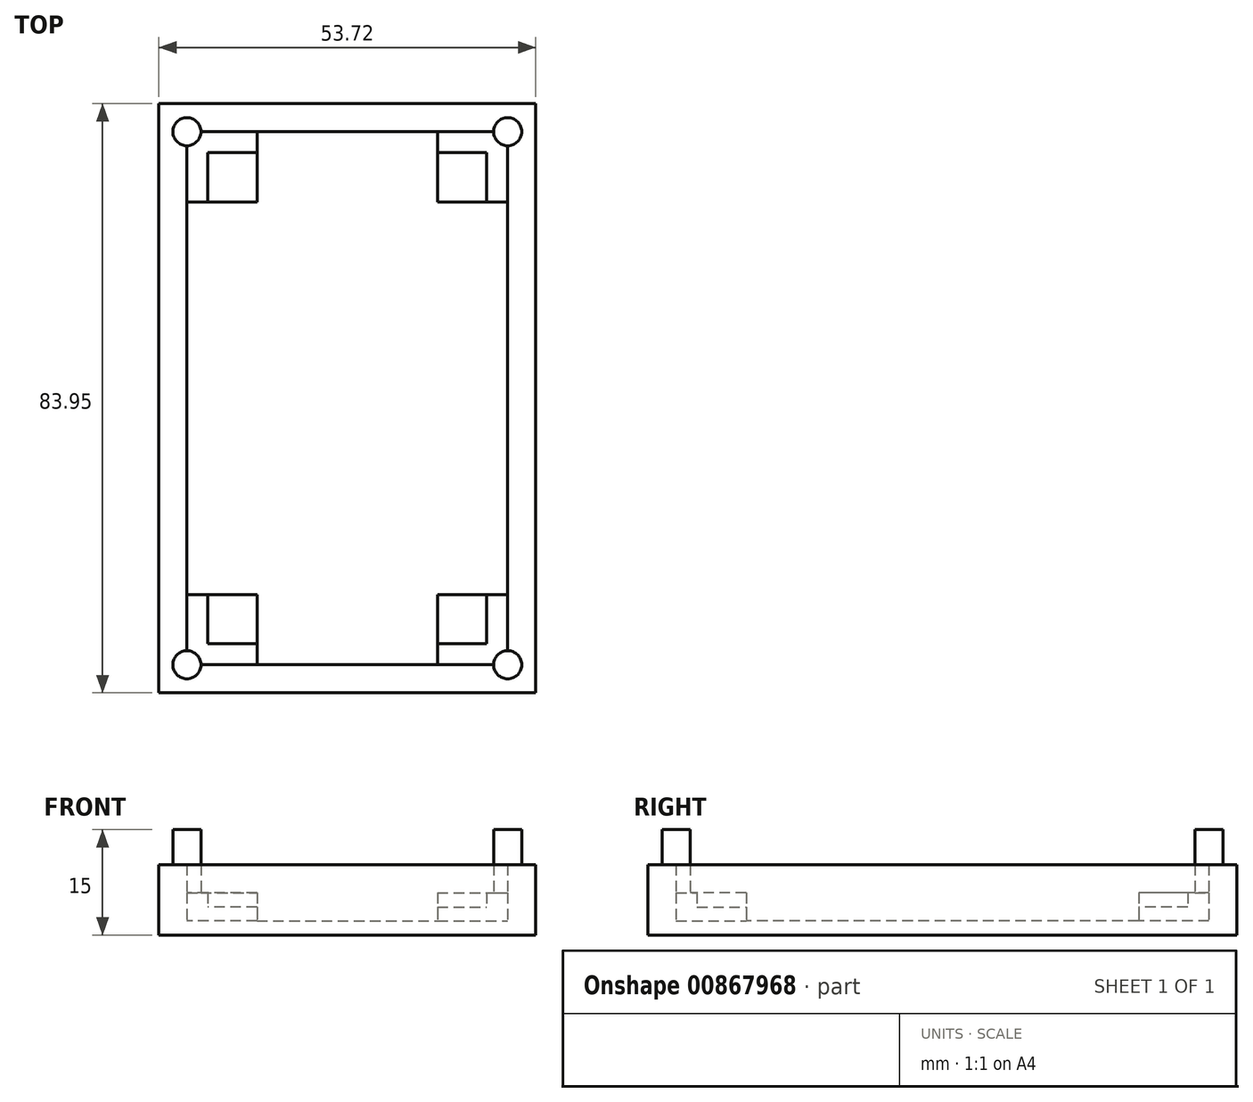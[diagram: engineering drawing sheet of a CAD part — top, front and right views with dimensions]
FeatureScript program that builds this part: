
annotation { "Feature Type Name" : "Feature", "Feature Type Description" : "" }
export const myFeature = defineFeature(function(context is Context, id is Id, definition is map)
    precondition{}
    {
        {
            var Q0;
            Q0=qCreatedBy(makeId("Top.planeOp"),FACE);
            var sketch = newSketch(context, id + "F0", { "sketchPlane" : qUnion([Q0])});
            skLineSegment(sketch, "E0.bottom", {"start": v(-27.14, 34.73) * mm, "end": v(26.58, 34.73) * mm});
            skLineSegment(sketch, "E0.top", {"start": v(-27.14, -49.22) * mm, "end": v(26.58, -49.22) * mm});
            skLineSegment(sketch, "E0.left", {"start": v(-27.14, 34.73) * mm, "end": v(-27.14, -49.22) * mm});
            skLineSegment(sketch, "E0.right", {"start": v(26.58, 34.73) * mm, "end": v(26.58, -49.22) * mm});
            skLineSegment(sketch, "E1.bottom", {"start": v(-23.14, 30.73) * mm, "end": v(22.58, 30.73) * mm});
            skLineSegment(sketch, "E1.top", {"start": v(-23.14, -45.22) * mm, "end": v(22.58, -45.22) * mm});
            skLineSegment(sketch, "E1.left", {"start": v(-23.14, 30.73) * mm, "end": v(-23.14, -45.22) * mm});
            skLineSegment(sketch, "E1.right", {"start": v(22.58, 30.73) * mm, "end": v(22.58, -45.22) * mm});
            skLineSegment(sketch, "E2", {"start": v(-23.14, 30.73) * mm, "end": v(-27.14, 30.73) * mm});
            skLineSegment(sketch, "E3", {"start": v(-23.14, 30.73) * mm, "end": v(-23.14, 34.73) * mm});
            skLineSegment(sketch, "E4", {"start": v(22.58, -45.22) * mm, "end": v(26.58, -45.22) * mm});
            skLineSegment(sketch, "E5", {"start": v(22.58, -45.22) * mm, "end": v(22.58, -49.22) * mm});
            skCircle(sketch, "E6", {"center": v(-23.14, 30.73) * mm, "radius": 2 * mm});
            skCircle(sketch, "E7", {"center": v(22.58, 30.73) * mm, "radius": 2 * mm});
            skCircle(sketch, "E8", {"center": v(22.58, -45.22) * mm, "radius": 2 * mm});
            skCircle(sketch, "E9", {"center": v(-23.14, -45.22) * mm, "radius": 2 * mm});
            skLineSegment(sketch, "E10", {"start": v(12.58, -45.22) * mm, "end": v(12.58, -35.22) * mm});
            skLineSegment(sketch, "E11", {"start": v(12.58, -35.22) * mm, "end": v(22.58, -35.22) * mm});
            skLineSegment(sketch, "E12", {"start": v(-13.14, -45.22) * mm, "end": v(-13.14, -35.22) * mm});
            skLineSegment(sketch, "E13", {"start": v(-13.14, -35.22) * mm, "end": v(-23.14, -35.22) * mm});
            skLineSegment(sketch, "E14", {"start": v(12.58, 30.73) * mm, "end": v(12.58, 20.73) * mm});
            skLineSegment(sketch, "E15", {"start": v(12.58, 20.73) * mm, "end": v(22.58, 20.73) * mm});
            skLineSegment(sketch, "E16", {"start": v(-13.14, 30.73) * mm, "end": v(-13.14, 20.73) * mm});
            skLineSegment(sketch, "E17", {"start": v(-13.14, 20.73) * mm, "end": v(-23.14, 20.73) * mm});
            skLineSegment(sketch, "E18", {"start": v(-20.14, -35.22) * mm, "end": v(-20.14, -42.22) * mm});
            skLineSegment(sketch, "E19", {"start": v(-20.14, -42.22) * mm, "end": v(-13.14, -42.22) * mm});
            skLineSegment(sketch, "E20", {"start": v(12.58, 27.73) * mm, "end": v(19.58, 27.73) * mm});
            skLineSegment(sketch, "E21", {"start": v(19.58, 27.73) * mm, "end": v(19.58, 20.73) * mm});
            skLineSegment(sketch, "E22", {"start": v(-13.14, 27.73) * mm, "end": v(-20.14, 27.73) * mm});
            skLineSegment(sketch, "E23", {"start": v(-20.14, 27.73) * mm, "end": v(-20.14, 20.73) * mm});
            skLineSegment(sketch, "E24", {"start": v(19.58, -42.22) * mm, "end": v(12.58, -42.22) * mm});
            skLineSegment(sketch, "E25", {"start": v(19.58, -42.22) * mm, "end": v(19.58, -35.22) * mm});
            skSolve(sketch);
        }
        {
            var Q0;
            {var subQ9=sQuery(id+"F0.wireOp",EDGE,"E0.right");var subQ10=sQuery(id+"F0.wireOp",EDGE,"E0.bottom");var subQ11=makeQuery(id+"F0.imprint","INTERSECT",VERTEX,{"derivedFrom":[subQ10,subQ9]});Q0=makeQuery(id+"F0.imprint","IMPRINT",FACE,{"disambiguationData":[TD([[makeQuery(id+"F0.imprint","IMPRINT",EDGE,{"disambiguationData":[TD([[subQ11,1.0]])],"derivedFrom":subQ10}),-1.0]])]});}
            var Q1;
            {var subQ1=sQuery(id+"F0.wireOp",EDGE,"E0.bottom");var subQ6=sQuery(id+"F0.wireOp",EDGE,"E0.left");var subQ9=makeQuery(id+"F0.imprint","INTERSECT",VERTEX,{"derivedFrom":[subQ1,subQ6]});Q1=makeQuery(id+"F0.imprint","IMPRINT",FACE,{"disambiguationData":[TD([[makeQuery(id+"F0.imprint","IMPRINT",EDGE,{"disambiguationData":[TD([[subQ9,-1.0]])],"derivedFrom":subQ1}),-1.0]])]});}
            var Q2;
            {var subQ5=sQuery(id+"F0.wireOp",EDGE,"E0.left");var subQ6=sQuery(id+"F0.wireOp",EDGE,"E0.top");var subQ7=makeQuery(id+"F0.imprint","INTERSECT",VERTEX,{"derivedFrom":[subQ6,subQ5]});Q2=makeQuery(id+"F0.imprint","IMPRINT",FACE,{"disambiguationData":[TD([[makeQuery(id+"F0.imprint","IMPRINT",EDGE,{"disambiguationData":[TD([[subQ7,-1.0]])],"derivedFrom":subQ6}),1.0]])]});}
            var Q3;
            {var subQ1=sQuery(id+"F0.wireOp",EDGE,"E0.right");var subQ5=sQuery(id+"F0.wireOp",EDGE,"E0.top");var subQ6=makeQuery(id+"F0.imprint","INTERSECT",VERTEX,{"derivedFrom":[subQ5,subQ1]});Q3=makeQuery(id+"F0.imprint","IMPRINT",FACE,{"disambiguationData":[TD([[makeQuery(id+"F0.imprint","IMPRINT",EDGE,{"disambiguationData":[TD([[subQ6,1.0]])],"derivedFrom":subQ5}),1.0]])]});}
            extrude(context, id + "F1", {"entities" : qUnion([Q0, Q1, Q2, Q3]), "depth" : 10 * mm, "offsetDistance" : 25 * mm});
        }
        {
            var Q0;
            {var subQ5=sQuery(id+"F0.wireOp",EDGE,"E6");var subQ13=sQuery(id+"F0.wireOp",EDGE,"E1.bottom");var subQ14=makeQuery(id+"F0.imprint","INTERSECT",VERTEX,{"derivedFrom":[subQ13,subQ5]});Q0=makeQuery(id+"F0.imprint","IMPRINT",FACE,{"disambiguationData":[TD([[makeQuery(id+"F0.imprint","IMPRINT",EDGE,{"disambiguationData":[TD([[subQ14,-1.0]])],"derivedFrom":subQ13}),-1.0]])]});}
            var Q1;
            {var subQ9=sQuery(id+"F0.wireOp",EDGE,"E20");Q1=makeQuery(id+"F0.imprint","IMPRINT",FACE,{"disambiguationData":[TD([[makeQuery(id+"F0.imprint","IMPRINT",EDGE,{"derivedFrom":subQ9}),1.0]])]});}
            var Q2;
            {var subQ3=sQuery(id+"F0.wireOp",EDGE,"E24");Q2=makeQuery(id+"F0.imprint","IMPRINT",FACE,{"disambiguationData":[TD([[makeQuery(id+"F0.imprint","IMPRINT",EDGE,{"derivedFrom":subQ3}),1.0]])]});}
            var Q3;
            {var subQ10=sQuery(id+"F0.wireOp",EDGE,"E18");Q3=makeQuery(id+"F0.imprint","IMPRINT",FACE,{"disambiguationData":[TD([[makeQuery(id+"F0.imprint","IMPRINT",EDGE,{"derivedFrom":subQ10}),-1.0]])]});}
            extrude(context, id + "F2", {"entities" : qUnion([Q0, Q1, Q2, Q3]), "operationType" : NewBodyOperationType.ADD, "depth" : 6 * mm, "offsetDistance" : 25 * mm});
        }
        {
            var Q0;
            {var subQ1=sQuery(id+"F0.wireOp",EDGE,"E1.bottom");var subQ3=sQuery(id+"F0.wireOp",EDGE,"E6");var subQ4=makeQuery(id+"F0.imprint","INTERSECT",VERTEX,{"derivedFrom":[subQ1,subQ3]});Q0=makeQuery(id+"F0.imprint","IMPRINT",FACE,{"disambiguationData":[TD([[makeQuery(id+"F0.imprint","IMPRINT",EDGE,{"disambiguationData":[TD([[subQ4,1.0]])],"derivedFrom":subQ3}),1.0]])]});}
            var Q1;
            {var subQ1=sQuery(id+"F0.wireOp",EDGE,"E2");var subQ3=sQuery(id+"F0.wireOp",EDGE,"E6");var subQ4=makeQuery(id+"F0.imprint","INTERSECT",VERTEX,{"derivedFrom":[subQ1,subQ3]});Q1=makeQuery(id+"F0.imprint","IMPRINT",FACE,{"disambiguationData":[TD([[makeQuery(id+"F0.imprint","IMPRINT",EDGE,{"disambiguationData":[TD([[subQ4,1.0]])],"derivedFrom":subQ3}),1.0]])]});}
            var Q2;
            {var subQ1=sQuery(id+"F0.wireOp",EDGE,"E1.bottom");var subQ3=sQuery(id+"F0.wireOp",EDGE,"E6");var subQ4=makeQuery(id+"F0.imprint","INTERSECT",VERTEX,{"derivedFrom":[subQ1,subQ3]});Q2=makeQuery(id+"F0.imprint","IMPRINT",FACE,{"disambiguationData":[TD([[makeQuery(id+"F0.imprint","IMPRINT",EDGE,{"disambiguationData":[TD([[subQ4,-1.0]])],"derivedFrom":subQ3}),1.0]])]});}
            var Q3;
            {var subQ1=sQuery(id+"F0.wireOp",EDGE,"E1.left");var subQ3=sQuery(id+"F0.wireOp",EDGE,"E6");var subQ4=makeQuery(id+"F0.imprint","INTERSECT",VERTEX,{"derivedFrom":[subQ1,subQ3]});Q3=makeQuery(id+"F0.imprint","IMPRINT",FACE,{"disambiguationData":[TD([[makeQuery(id+"F0.imprint","IMPRINT",EDGE,{"disambiguationData":[TD([[subQ4,1.0]])],"derivedFrom":subQ3}),1.0]])]});}
            var Q4;
            {var subQ0=sQuery(id+"F0.wireOp",EDGE,"E1.right");var subQ1=sQuery(id+"F0.wireOp",EDGE,"E1.bottom");var subQ2=makeQuery(id+"F0.imprint","INTERSECT",VERTEX,{"derivedFrom":[subQ1,subQ0]});Q4=makeQuery(id+"F0.imprint","IMPRINT",FACE,{"disambiguationData":[TD([[makeQuery(id+"F0.imprint","IMPRINT",EDGE,{"disambiguationData":[TD([[subQ2,1.0]])],"derivedFrom":subQ1}),1.0]])]});}
            var Q5;
            {var subQ0=sQuery(id+"F0.wireOp",EDGE,"E1.right");var subQ1=sQuery(id+"F0.wireOp",EDGE,"E1.bottom");var subQ2=makeQuery(id+"F0.imprint","INTERSECT",VERTEX,{"derivedFrom":[subQ1,subQ0]});Q5=makeQuery(id+"F0.imprint","IMPRINT",FACE,{"disambiguationData":[TD([[makeQuery(id+"F0.imprint","IMPRINT",EDGE,{"disambiguationData":[TD([[subQ2,1.0]])],"derivedFrom":subQ1}),-1.0]])]});}
            var Q6;
            {var subQ1=sQuery(id+"F0.wireOp",EDGE,"E1.top");var subQ3=sQuery(id+"F0.wireOp",EDGE,"E8");var subQ4=makeQuery(id+"F0.imprint","INTERSECT",VERTEX,{"derivedFrom":[subQ1,subQ3]});Q6=makeQuery(id+"F0.imprint","IMPRINT",FACE,{"disambiguationData":[TD([[makeQuery(id+"F0.imprint","IMPRINT",EDGE,{"disambiguationData":[TD([[subQ4,1.0]])],"derivedFrom":subQ3}),1.0]])]});}
            var Q7;
            {var subQ1=sQuery(id+"F0.wireOp",EDGE,"E1.right");var subQ3=sQuery(id+"F0.wireOp",EDGE,"E8");var subQ4=makeQuery(id+"F0.imprint","INTERSECT",VERTEX,{"derivedFrom":[subQ1,subQ3]});Q7=makeQuery(id+"F0.imprint","IMPRINT",FACE,{"disambiguationData":[TD([[makeQuery(id+"F0.imprint","IMPRINT",EDGE,{"disambiguationData":[TD([[subQ4,1.0]])],"derivedFrom":subQ3}),1.0]])]});}
            var Q8;
            {var subQ1=sQuery(id+"F0.wireOp",EDGE,"E4");var subQ3=sQuery(id+"F0.wireOp",EDGE,"E8");var subQ4=makeQuery(id+"F0.imprint","INTERSECT",VERTEX,{"derivedFrom":[subQ1,subQ3]});Q8=makeQuery(id+"F0.imprint","IMPRINT",FACE,{"disambiguationData":[TD([[makeQuery(id+"F0.imprint","IMPRINT",EDGE,{"disambiguationData":[TD([[subQ4,1.0]])],"derivedFrom":subQ3}),1.0]])]});}
            var Q9;
            {var subQ1=sQuery(id+"F0.wireOp",EDGE,"E1.top");var subQ3=sQuery(id+"F0.wireOp",EDGE,"E8");var subQ4=makeQuery(id+"F0.imprint","INTERSECT",VERTEX,{"derivedFrom":[subQ1,subQ3]});Q9=makeQuery(id+"F0.imprint","IMPRINT",FACE,{"disambiguationData":[TD([[makeQuery(id+"F0.imprint","IMPRINT",EDGE,{"disambiguationData":[TD([[subQ4,-1.0]])],"derivedFrom":subQ3}),1.0]])]});}
            var Q10;
            {var subQ0=sQuery(id+"F0.wireOp",EDGE,"E1.left");var subQ1=sQuery(id+"F0.wireOp",EDGE,"E1.top");var subQ2=makeQuery(id+"F0.imprint","INTERSECT",VERTEX,{"derivedFrom":[subQ1,subQ0]});Q10=makeQuery(id+"F0.imprint","IMPRINT",FACE,{"disambiguationData":[TD([[makeQuery(id+"F0.imprint","IMPRINT",EDGE,{"disambiguationData":[TD([[subQ2,-1.0]])],"derivedFrom":subQ1}),1.0]])]});}
            var Q11;
            {var subQ0=sQuery(id+"F0.wireOp",EDGE,"E1.left");var subQ1=sQuery(id+"F0.wireOp",EDGE,"E1.top");var subQ2=makeQuery(id+"F0.imprint","INTERSECT",VERTEX,{"derivedFrom":[subQ1,subQ0]});Q11=makeQuery(id+"F0.imprint","IMPRINT",FACE,{"disambiguationData":[TD([[makeQuery(id+"F0.imprint","IMPRINT",EDGE,{"disambiguationData":[TD([[subQ2,-1.0]])],"derivedFrom":subQ1}),-1.0]])]});}
            extrude(context, id + "F3", {"entities" : qUnion([Q0, Q1, Q2, Q3, Q4, Q5, Q6, Q7, Q8, Q9, Q10, Q11]), "operationType" : NewBodyOperationType.ADD, "depth" : 15 * mm, "offsetDistance" : 25 * mm});
        }
        {
            var Q0;
            {var subQ3=sQuery(id+"F0.wireOp",EDGE,"E22");Q0=makeQuery(id+"F0.imprint","IMPRINT",FACE,{"disambiguationData":[TD([[makeQuery(id+"F0.imprint","IMPRINT",EDGE,{"derivedFrom":subQ3}),1.0]])]});}
            var Q1;
            {var subQ3=sQuery(id+"F0.wireOp",EDGE,"E20");Q1=makeQuery(id+"F0.imprint","IMPRINT",FACE,{"disambiguationData":[TD([[makeQuery(id+"F0.imprint","IMPRINT",EDGE,{"derivedFrom":subQ3}),-1.0]])]});}
            var Q2;
            {var subQ3=sQuery(id+"F0.wireOp",EDGE,"E24");Q2=makeQuery(id+"F0.imprint","IMPRINT",FACE,{"disambiguationData":[TD([[makeQuery(id+"F0.imprint","IMPRINT",EDGE,{"derivedFrom":subQ3}),-1.0]])]});}
            var Q3;
            {var subQ4=sQuery(id+"F0.wireOp",EDGE,"E18");Q3=makeQuery(id+"F0.imprint","IMPRINT",FACE,{"disambiguationData":[TD([[makeQuery(id+"F0.imprint","IMPRINT",EDGE,{"derivedFrom":subQ4}),1.0]])]});}
            extrude(context, id + "F4", {"entities" : qUnion([Q0, Q1, Q2, Q3]), "operationType" : NewBodyOperationType.ADD, "depth" : 4 * mm, "offsetDistance" : 25 * mm});
        }
        {
            var Q0;
            {var subQ11=sQuery(id+"F0.wireOp",EDGE,"E14");var subQ12=sQuery(id+"F0.wireOp",EDGE,"E1.bottom");var subQ13=makeQuery(id+"F0.imprint","INTERSECT",VERTEX,{"derivedFrom":[subQ12,subQ11]});Q0=makeQuery(id+"F0.imprint","IMPRINT",FACE,{"disambiguationData":[TD([[makeQuery(id+"F0.imprint","IMPRINT",EDGE,{"disambiguationData":[TD([[subQ13,1.0]])],"derivedFrom":subQ12}),-1.0]])]});}
            extrude(context, id + "F5", {"entities" : qUnion([Q0]), "operationType" : NewBodyOperationType.ADD, "depth" : 2 * mm, "offsetDistance" : 25 * mm});
        }
    });
